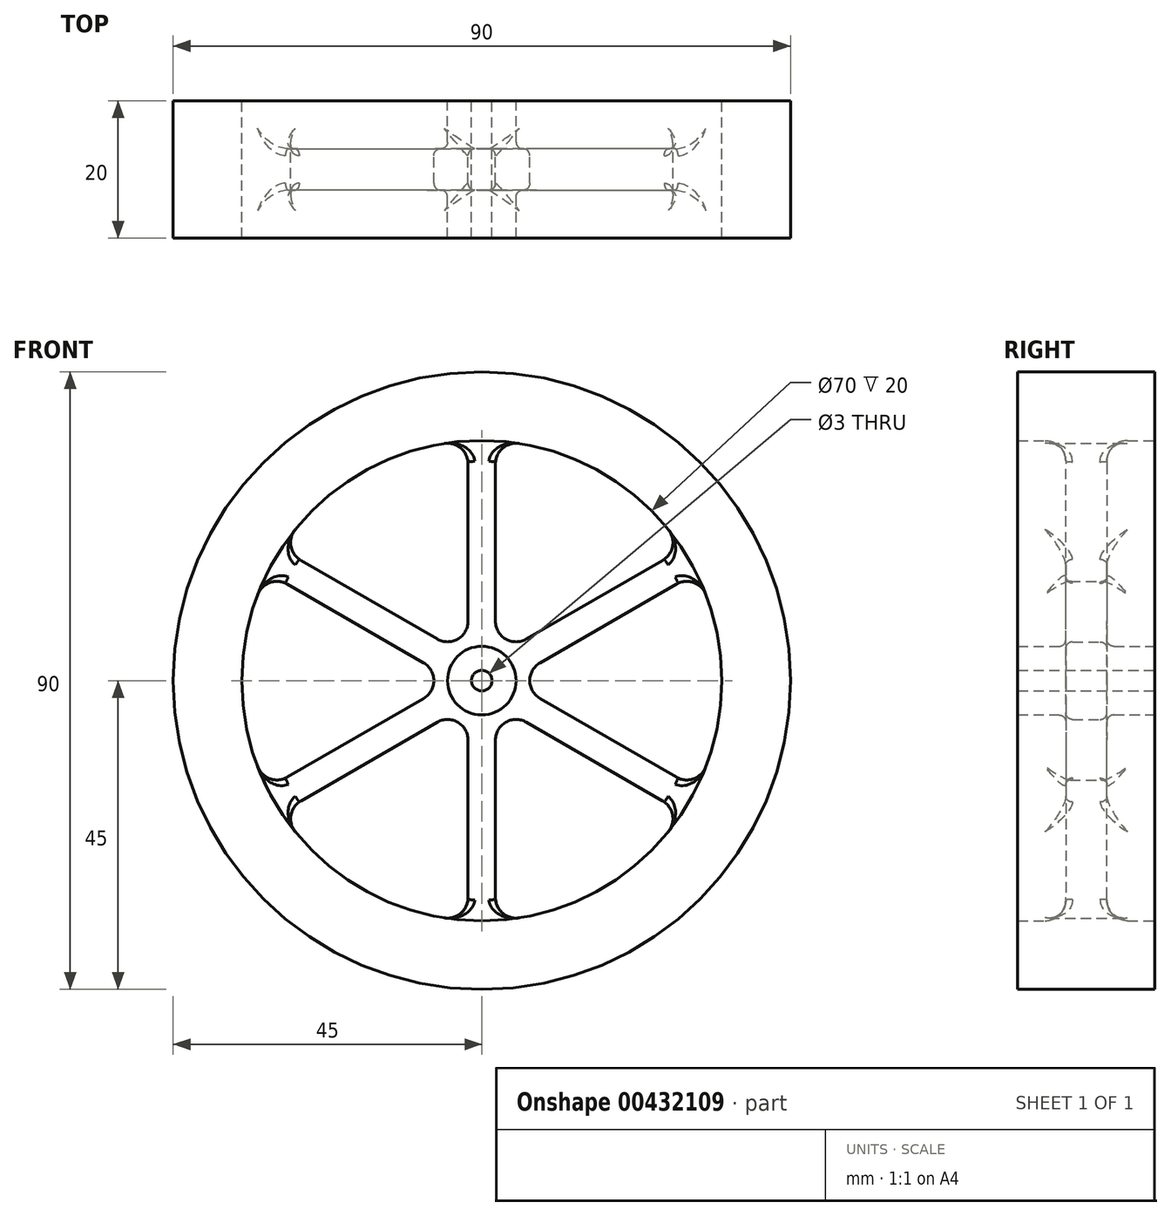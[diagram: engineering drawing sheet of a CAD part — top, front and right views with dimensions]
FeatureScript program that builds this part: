
annotation { "Feature Type Name" : "Feature", "Feature Type Description" : "" }
export const myFeature = defineFeature(function(context is Context, id is Id, definition is map)
    precondition{}
    {
        {
            var Q0;
            Q0=qCreatedBy(makeId("Front.planeOp"),FACE);
            var sketch = newSketch(context, id + "F0", { "sketchPlane" : qUnion([Q0])});
            skCircle(sketch, "E0", {"center": v(0, 0) * mm, "radius": 45 * mm});
            skArc(sketch, "E1", {"start": v(-32.67, 12.55) * mm, "mid": v(-35, 0) * mm, "end": v(-32.67, -12.55) * mm});
            skLineSegment(sketch, "E2.0", {"start": v(2, 8.66) * mm, "end": v(2, 31.6) * mm});
            skLineSegment(sketch, "E3.0", {"start": v(-2, 8.66) * mm, "end": v(-2, 31.6) * mm});
            skLineSegment(sketch, "E4.1.0", {"start": v(-8.5, 2.6) * mm, "end": v(-28.37, 14.07) * mm});
            skLineSegment(sketch, "E4.1.1", {"start": v(-6.5, 6.06) * mm, "end": v(-26.37, 17.54) * mm});
            skLineSegment(sketch, "E4.2.0", {"start": v(-6.5, -6.06) * mm, "end": v(-26.37, -17.54) * mm});
            skLineSegment(sketch, "E4.2.1", {"start": v(-8.5, -2.6) * mm, "end": v(-28.37, -14.07) * mm});
            skLineSegment(sketch, "E4.3.0", {"start": v(2, -8.66) * mm, "end": v(2, -31.6) * mm});
            skLineSegment(sketch, "E4.3.1", {"start": v(-2, -8.66) * mm, "end": v(-2, -31.6) * mm});
            skLineSegment(sketch, "E4.4.0", {"start": v(8.5, -2.6) * mm, "end": v(28.37, -14.07) * mm});
            skLineSegment(sketch, "E4.4.1", {"start": v(6.5, -6.06) * mm, "end": v(26.37, -17.54) * mm});
            skLineSegment(sketch, "E4.5.0", {"start": v(6.5, 6.06) * mm, "end": v(26.37, 17.54) * mm});
            skLineSegment(sketch, "E4.5.1", {"start": v(8.5, 2.6) * mm, "end": v(28.37, 14.07) * mm});
            skArc(sketch, "E5.filletArc", {"start": v(2, 8.66) * mm, "mid": v(3.5, 6.06) * mm, "end": v(6.5, 6.06) * mm});
            skArc(sketch, "E6.filletArc", {"start": v(-6.5, 6.06) * mm, "mid": v(-3.5, 6.06) * mm, "end": v(-2, 8.66) * mm});
            skArc(sketch, "E7.filletArc", {"start": v(-8.5, -2.6) * mm, "mid": v(-7, 0) * mm, "end": v(-8.5, 2.6) * mm});
            skArc(sketch, "E8.filletArc", {"start": v(-2, -8.66) * mm, "mid": v(-3.5, -6.06) * mm, "end": v(-6.5, -6.06) * mm});
            skArc(sketch, "E9.filletArc", {"start": v(6.5, -6.06) * mm, "mid": v(3.5, -6.06) * mm, "end": v(2, -8.66) * mm});
            skArc(sketch, "E10.filletArc", {"start": v(8.5, 2.6) * mm, "mid": v(7, 0) * mm, "end": v(8.5, -2.6) * mm});
            skArc(sketch, "E11.trimOffspring", {"start": v(-5.47, 34.57) * mm, "mid": v(-17.5, 30.31) * mm, "end": v(-27.2, 22.02) * mm});
            skArc(sketch, "E12.trimOffspring", {"start": v(27.2, 22.02) * mm, "mid": v(17.5, 30.31) * mm, "end": v(5.47, 34.57) * mm});
            skArc(sketch, "E13.trimOffspring", {"start": v(32.67, -12.55) * mm, "mid": v(35, 0) * mm, "end": v(32.67, 12.55) * mm});
            skArc(sketch, "E14.trimOffspring", {"start": v(5.47, -34.57) * mm, "mid": v(17.5, -30.31) * mm, "end": v(27.2, -22.02) * mm});
            skArc(sketch, "E15.trimOffspring", {"start": v(-27.2, -22.02) * mm, "mid": v(-17.5, -30.31) * mm, "end": v(-5.47, -34.57) * mm});
            skArc(sketch, "E16.filletArc", {"start": v(-27.2, 22.02) * mm, "mid": v(-27.82, 19.59) * mm, "end": v(-26.37, 17.54) * mm});
            skArc(sketch, "E17.filletArc", {"start": v(-2, 31.6) * mm, "mid": v(-3.05, 33.89) * mm, "end": v(-5.47, 34.57) * mm});
            skArc(sketch, "E18.filletArc", {"start": v(5.47, 34.57) * mm, "mid": v(3.05, 33.89) * mm, "end": v(2, 31.6) * mm});
            skArc(sketch, "E19.filletArc", {"start": v(26.37, 17.54) * mm, "mid": v(27.82, 19.59) * mm, "end": v(27.2, 22.02) * mm});
            skArc(sketch, "E20.filletArc", {"start": v(32.67, 12.55) * mm, "mid": v(30.87, 14.3) * mm, "end": v(28.37, 14.07) * mm});
            skArc(sketch, "E21.filletArc", {"start": v(28.37, -14.07) * mm, "mid": v(30.87, -14.3) * mm, "end": v(32.67, -12.55) * mm});
            skArc(sketch, "E22.filletArc", {"start": v(27.2, -22.02) * mm, "mid": v(27.82, -19.59) * mm, "end": v(26.37, -17.54) * mm});
            skArc(sketch, "E23.filletArc", {"start": v(2, -31.6) * mm, "mid": v(3.05, -33.89) * mm, "end": v(5.47, -34.57) * mm});
            skArc(sketch, "E24.filletArc", {"start": v(-5.47, -34.57) * mm, "mid": v(-3.05, -33.89) * mm, "end": v(-2, -31.6) * mm});
            skArc(sketch, "E25.filletArc", {"start": v(-26.37, -17.54) * mm, "mid": v(-27.82, -19.59) * mm, "end": v(-27.2, -22.02) * mm});
            skArc(sketch, "E26.filletArc", {"start": v(-32.67, -12.55) * mm, "mid": v(-30.87, -14.3) * mm, "end": v(-28.37, -14.07) * mm});
            skArc(sketch, "E27.filletArc", {"start": v(-28.37, 14.07) * mm, "mid": v(-30.87, 14.3) * mm, "end": v(-32.67, 12.55) * mm});
            skSolve(sketch);
        }
        {
            var Q0;
            Q0 = qSketchRegion(id + "F0", true);
            extrude(context, id + "F1", {"entities" : qUnion([Q0]), "depth" : 20 * mm});
        }
        {
            var Q0;
            Q0=makeQuery(id+"F1.opExtrude","CAP_FACE",FACE,{"disambiguationData":[OSD([sQuery(id+"F0.wireOp",EDGE,"E0"),sQuery(id+"F0.wireOp",EDGE,"E1"),sQuery(id+"F0.wireOp",EDGE,"E2.0"),sQuery(id+"F0.wireOp",EDGE,"E3.0"),sQuery(id+"F0.wireOp",EDGE,"E4.1.0"),sQuery(id+"F0.wireOp",EDGE,"E4.1.1"),sQuery(id+"F0.wireOp",EDGE,"E4.2.0"),sQuery(id+"F0.wireOp",EDGE,"E4.2.1"),sQuery(id+"F0.wireOp",EDGE,"E4.3.0"),sQuery(id+"F0.wireOp",EDGE,"E4.3.1"),sQuery(id+"F0.wireOp",EDGE,"E4.4.0"),sQuery(id+"F0.wireOp",EDGE,"E4.4.1"),sQuery(id+"F0.wireOp",EDGE,"E4.5.0"),sQuery(id+"F0.wireOp",EDGE,"E4.5.1"),sQuery(id+"F0.wireOp",EDGE,"E5.filletArc"),sQuery(id+"F0.wireOp",EDGE,"E6.filletArc"),sQuery(id+"F0.wireOp",EDGE,"E7.filletArc"),sQuery(id+"F0.wireOp",EDGE,"E8.filletArc"),sQuery(id+"F0.wireOp",EDGE,"E9.filletArc"),sQuery(id+"F0.wireOp",EDGE,"E10.filletArc"),sQuery(id+"F0.wireOp",EDGE,"E11.trimOffspring"),sQuery(id+"F0.wireOp",EDGE,"E12.trimOffspring"),sQuery(id+"F0.wireOp",EDGE,"E13.trimOffspring"),sQuery(id+"F0.wireOp",EDGE,"E14.trimOffspring"),sQuery(id+"F0.wireOp",EDGE,"E15.trimOffspring"),sQuery(id+"F0.wireOp",EDGE,"E16.filletArc"),sQuery(id+"F0.wireOp",EDGE,"E17.filletArc"),sQuery(id+"F0.wireOp",EDGE,"E18.filletArc"),sQuery(id+"F0.wireOp",EDGE,"E19.filletArc"),sQuery(id+"F0.wireOp",EDGE,"E20.filletArc"),sQuery(id+"F0.wireOp",EDGE,"E21.filletArc"),sQuery(id+"F0.wireOp",EDGE,"E22.filletArc"),sQuery(id+"F0.wireOp",EDGE,"E23.filletArc"),sQuery(id+"F0.wireOp",EDGE,"E24.filletArc"),sQuery(id+"F0.wireOp",EDGE,"E25.filletArc"),sQuery(id+"F0.wireOp",EDGE,"E26.filletArc"),sQuery(id+"F0.wireOp",EDGE,"E27.filletArc")])],"isStart":false});
            var sketch = newSketch(context, id + "F2", { "sketchPlane" : qUnion([Q0])});
            skCircle(sketch, "E28", {"center": v(0, 0) * mm, "radius": 35 * mm});
            skSolve(sketch);
        }
        {
            var Q0;
            Q0 = qSketchRegion(id + "F2", true);
            extrude(context, id + "F3", {"entities" : qUnion([Q0]), "operationType" : NewBodyOperationType.REMOVE, "oppositeDirection" : true, "depth" : 7 * mm});
        }
        {
            var Q0;
            Q0=makeQuery(id+"F1.opExtrude","CAP_FACE",FACE,{"disambiguationData":[OSD([sQuery(id+"F0.wireOp",EDGE,"E0"),sQuery(id+"F0.wireOp",EDGE,"E1"),sQuery(id+"F0.wireOp",EDGE,"E2.0"),sQuery(id+"F0.wireOp",EDGE,"E3.0"),sQuery(id+"F0.wireOp",EDGE,"E4.1.0"),sQuery(id+"F0.wireOp",EDGE,"E4.1.1"),sQuery(id+"F0.wireOp",EDGE,"E4.2.0"),sQuery(id+"F0.wireOp",EDGE,"E4.2.1"),sQuery(id+"F0.wireOp",EDGE,"E4.3.0"),sQuery(id+"F0.wireOp",EDGE,"E4.3.1"),sQuery(id+"F0.wireOp",EDGE,"E4.4.0"),sQuery(id+"F0.wireOp",EDGE,"E4.4.1"),sQuery(id+"F0.wireOp",EDGE,"E4.5.0"),sQuery(id+"F0.wireOp",EDGE,"E4.5.1"),sQuery(id+"F0.wireOp",EDGE,"E5.filletArc"),sQuery(id+"F0.wireOp",EDGE,"E6.filletArc"),sQuery(id+"F0.wireOp",EDGE,"E7.filletArc"),sQuery(id+"F0.wireOp",EDGE,"E8.filletArc"),sQuery(id+"F0.wireOp",EDGE,"E9.filletArc"),sQuery(id+"F0.wireOp",EDGE,"E10.filletArc"),sQuery(id+"F0.wireOp",EDGE,"E11.trimOffspring"),sQuery(id+"F0.wireOp",EDGE,"E12.trimOffspring"),sQuery(id+"F0.wireOp",EDGE,"E13.trimOffspring"),sQuery(id+"F0.wireOp",EDGE,"E14.trimOffspring"),sQuery(id+"F0.wireOp",EDGE,"E15.trimOffspring"),sQuery(id+"F0.wireOp",EDGE,"E16.filletArc"),sQuery(id+"F0.wireOp",EDGE,"E17.filletArc"),sQuery(id+"F0.wireOp",EDGE,"E18.filletArc"),sQuery(id+"F0.wireOp",EDGE,"E19.filletArc"),sQuery(id+"F0.wireOp",EDGE,"E20.filletArc"),sQuery(id+"F0.wireOp",EDGE,"E21.filletArc"),sQuery(id+"F0.wireOp",EDGE,"E22.filletArc"),sQuery(id+"F0.wireOp",EDGE,"E23.filletArc"),sQuery(id+"F0.wireOp",EDGE,"E24.filletArc"),sQuery(id+"F0.wireOp",EDGE,"E25.filletArc"),sQuery(id+"F0.wireOp",EDGE,"E26.filletArc"),sQuery(id+"F0.wireOp",EDGE,"E27.filletArc")])],"isStart":true});
            var sketch = newSketch(context, id + "F4", { "sketchPlane" : qUnion([Q0])});
            skCircle(sketch, "E29", {"center": v(0, 0) * mm, "radius": 35 * mm});
            skSolve(sketch);
        }
        {
            var Q0;
            Q0 = qSketchRegion(id + "F4", true);
            extrude(context, id + "F5", {"entities" : qUnion([Q0]), "operationType" : NewBodyOperationType.REMOVE, "oppositeDirection" : true, "depth" : 7 * mm});
        }
        {
            var Q0;
            {var subQ0=sQuery(id+"F4.wireOp",EDGE,"E29");Q0=makeQuery(id+"F5.boolean.opBoolean","COPY",EDGE,{"disambiguationData":[TD([makeQuery(id+"F1.opExtrude","SWEPT_FACE",FACE,{"disambiguationData":[OSD([sQuery(id+"F0.wireOp",EDGE,"E23.filletArc")])]})])],"derivedFrom":makeQuery(id+"F5.opExtrude","CAP_EDGE",EDGE,{"disambiguationData":[OSD([subQ0])],"isStart":false})});}
            var Q1;
            {var subQ0=sQuery(id+"F4.wireOp",EDGE,"E29");Q1=makeQuery(id+"F5.boolean.opBoolean","COPY",EDGE,{"disambiguationData":[TD([makeQuery(id+"F1.opExtrude","SWEPT_FACE",FACE,{"disambiguationData":[OSD([sQuery(id+"F0.wireOp",EDGE,"E21.filletArc")])]})])],"derivedFrom":makeQuery(id+"F5.opExtrude","CAP_EDGE",EDGE,{"disambiguationData":[OSD([subQ0])],"isStart":false})});}
            var Q2;
            {var subQ0=sQuery(id+"F4.wireOp",EDGE,"E29");Q2=makeQuery(id+"F5.boolean.opBoolean","COPY",EDGE,{"disambiguationData":[TD([makeQuery(id+"F1.opExtrude","SWEPT_FACE",FACE,{"disambiguationData":[OSD([sQuery(id+"F0.wireOp",EDGE,"E19.filletArc")])]})])],"derivedFrom":makeQuery(id+"F5.opExtrude","CAP_EDGE",EDGE,{"disambiguationData":[OSD([subQ0])],"isStart":false})});}
            var Q3;
            {var subQ0=sQuery(id+"F4.wireOp",EDGE,"E29");Q3=makeQuery(id+"F5.boolean.opBoolean","COPY",EDGE,{"disambiguationData":[TD([makeQuery(id+"F1.opExtrude","SWEPT_FACE",FACE,{"disambiguationData":[OSD([sQuery(id+"F0.wireOp",EDGE,"E17.filletArc")])]})])],"derivedFrom":makeQuery(id+"F5.opExtrude","CAP_EDGE",EDGE,{"disambiguationData":[OSD([subQ0])],"isStart":false})});}
            var Q4;
            {var subQ0=sQuery(id+"F4.wireOp",EDGE,"E29");Q4=makeQuery(id+"F5.boolean.opBoolean","COPY",EDGE,{"disambiguationData":[TD([makeQuery(id+"F1.opExtrude","SWEPT_FACE",FACE,{"disambiguationData":[OSD([sQuery(id+"F0.wireOp",EDGE,"E16.filletArc")])]})])],"derivedFrom":makeQuery(id+"F5.opExtrude","CAP_EDGE",EDGE,{"disambiguationData":[OSD([subQ0])],"isStart":false})});}
            var Q5;
            {var subQ0=sQuery(id+"F4.wireOp",EDGE,"E29");Q5=makeQuery(id+"F5.boolean.opBoolean","COPY",EDGE,{"disambiguationData":[TD([makeQuery(id+"F1.opExtrude","SWEPT_FACE",FACE,{"disambiguationData":[OSD([sQuery(id+"F0.wireOp",EDGE,"E25.filletArc")])]})])],"derivedFrom":makeQuery(id+"F5.opExtrude","CAP_EDGE",EDGE,{"disambiguationData":[OSD([subQ0])],"isStart":false})});}
            var Q6;
            {var subQ0=sQuery(id+"F2.wireOp",EDGE,"E28");Q6=makeQuery(id+"F3.boolean.opBoolean","COPY",EDGE,{"disambiguationData":[TD([makeQuery(id+"F1.opExtrude","SWEPT_FACE",FACE,{"disambiguationData":[OSD([sQuery(id+"F0.wireOp",EDGE,"E21.filletArc")])]})])],"derivedFrom":makeQuery(id+"F3.opExtrude","CAP_EDGE",EDGE,{"disambiguationData":[OSD([subQ0])],"isStart":false})});}
            var Q7;
            {var subQ0=sQuery(id+"F2.wireOp",EDGE,"E28");Q7=makeQuery(id+"F3.boolean.opBoolean","COPY",EDGE,{"disambiguationData":[TD([makeQuery(id+"F1.opExtrude","SWEPT_FACE",FACE,{"disambiguationData":[OSD([sQuery(id+"F0.wireOp",EDGE,"E23.filletArc")])]})])],"derivedFrom":makeQuery(id+"F3.opExtrude","CAP_EDGE",EDGE,{"disambiguationData":[OSD([subQ0])],"isStart":false})});}
            var Q8;
            {var subQ0=sQuery(id+"F2.wireOp",EDGE,"E28");Q8=makeQuery(id+"F3.boolean.opBoolean","COPY",EDGE,{"disambiguationData":[TD([makeQuery(id+"F1.opExtrude","SWEPT_FACE",FACE,{"disambiguationData":[OSD([sQuery(id+"F0.wireOp",EDGE,"E25.filletArc")])]})])],"derivedFrom":makeQuery(id+"F3.opExtrude","CAP_EDGE",EDGE,{"disambiguationData":[OSD([subQ0])],"isStart":false})});}
            var Q9;
            {var subQ0=sQuery(id+"F2.wireOp",EDGE,"E28");Q9=makeQuery(id+"F3.boolean.opBoolean","COPY",EDGE,{"disambiguationData":[TD([makeQuery(id+"F1.opExtrude","SWEPT_FACE",FACE,{"disambiguationData":[OSD([sQuery(id+"F0.wireOp",EDGE,"E16.filletArc")])]})])],"derivedFrom":makeQuery(id+"F3.opExtrude","CAP_EDGE",EDGE,{"disambiguationData":[OSD([subQ0])],"isStart":false})});}
            var Q10;
            {var subQ0=sQuery(id+"F2.wireOp",EDGE,"E28");Q10=makeQuery(id+"F3.boolean.opBoolean","COPY",EDGE,{"disambiguationData":[TD([makeQuery(id+"F1.opExtrude","SWEPT_FACE",FACE,{"disambiguationData":[OSD([sQuery(id+"F0.wireOp",EDGE,"E17.filletArc")])]})])],"derivedFrom":makeQuery(id+"F3.opExtrude","CAP_EDGE",EDGE,{"disambiguationData":[OSD([subQ0])],"isStart":false})});}
            var Q11;
            {var subQ0=sQuery(id+"F2.wireOp",EDGE,"E28");Q11=makeQuery(id+"F3.boolean.opBoolean","COPY",EDGE,{"disambiguationData":[TD([makeQuery(id+"F1.opExtrude","SWEPT_FACE",FACE,{"disambiguationData":[OSD([sQuery(id+"F0.wireOp",EDGE,"E19.filletArc")])]})])],"derivedFrom":makeQuery(id+"F3.opExtrude","CAP_EDGE",EDGE,{"disambiguationData":[OSD([subQ0])],"isStart":false})});}
            fillet(context, id + "F6", {"entities" : qUnion([Q0, Q1, Q2, Q3, Q4, Q5, Q6, Q7, Q8, Q9, Q10, Q11]), "radius" : 3 * mm, "tangentPropagation" : true, "allowEdgeOverflow" : false});
        }
        {
            var Q0;
            Q0=makeQuery(id+"F5.boolean.opBoolean","INTERSECT",EDGE,{"derivedFrom":[makeQuery(id+"F1.opExtrude","SWEPT_FACE",FACE,{"disambiguationData":[OSD([sQuery(id+"F0.wireOp",EDGE,"E3.0")])]}),makeQuery(id+"F5.opExtrude","CAP_FACE",FACE,{"disambiguationData":[OSD([sQuery(id+"F4.wireOp",EDGE,"E29")])],"isStart":false})]});
            var Q1;
            Q1=makeQuery(id+"F5.boolean.opBoolean","INTERSECT",EDGE,{"derivedFrom":[makeQuery(id+"F1.opExtrude","SWEPT_FACE",FACE,{"disambiguationData":[OSD([sQuery(id+"F0.wireOp",EDGE,"E4.1.0")])]}),makeQuery(id+"F5.opExtrude","CAP_FACE",FACE,{"disambiguationData":[OSD([sQuery(id+"F4.wireOp",EDGE,"E29")])],"isStart":false})]});
            var Q2;
            Q2=makeQuery(id+"F5.boolean.opBoolean","INTERSECT",EDGE,{"derivedFrom":[makeQuery(id+"F1.opExtrude","SWEPT_FACE",FACE,{"disambiguationData":[OSD([sQuery(id+"F0.wireOp",EDGE,"E4.2.0")])]}),makeQuery(id+"F5.opExtrude","CAP_FACE",FACE,{"disambiguationData":[OSD([sQuery(id+"F4.wireOp",EDGE,"E29")])],"isStart":false})]});
            var Q3;
            Q3=makeQuery(id+"F5.boolean.opBoolean","INTERSECT",EDGE,{"derivedFrom":[makeQuery(id+"F1.opExtrude","SWEPT_FACE",FACE,{"disambiguationData":[OSD([sQuery(id+"F0.wireOp",EDGE,"E4.3.0")])]}),makeQuery(id+"F5.opExtrude","CAP_FACE",FACE,{"disambiguationData":[OSD([sQuery(id+"F4.wireOp",EDGE,"E29")])],"isStart":false})]});
            var Q4;
            Q4=makeQuery(id+"F5.boolean.opBoolean","INTERSECT",EDGE,{"derivedFrom":[makeQuery(id+"F1.opExtrude","SWEPT_FACE",FACE,{"disambiguationData":[OSD([sQuery(id+"F0.wireOp",EDGE,"E4.5.1")])]}),makeQuery(id+"F5.opExtrude","CAP_FACE",FACE,{"disambiguationData":[OSD([sQuery(id+"F4.wireOp",EDGE,"E29")])],"isStart":false})]});
            var Q5;
            Q5=makeQuery(id+"F5.boolean.opBoolean","INTERSECT",EDGE,{"derivedFrom":[makeQuery(id+"F1.opExtrude","SWEPT_FACE",FACE,{"disambiguationData":[OSD([sQuery(id+"F0.wireOp",EDGE,"E2.0")])]}),makeQuery(id+"F5.opExtrude","CAP_FACE",FACE,{"disambiguationData":[OSD([sQuery(id+"F4.wireOp",EDGE,"E29")])],"isStart":false})]});
            var Q6;
            Q6=makeQuery(id+"F3.boolean.opBoolean","INTERSECT",EDGE,{"derivedFrom":[makeQuery(id+"F1.opExtrude","SWEPT_FACE",FACE,{"disambiguationData":[OSD([sQuery(id+"F0.wireOp",EDGE,"E3.0")])]}),makeQuery(id+"F3.opExtrude","CAP_FACE",FACE,{"disambiguationData":[OSD([sQuery(id+"F2.wireOp",EDGE,"E28")])],"isStart":false})]});
            var Q7;
            Q7=makeQuery(id+"F3.boolean.opBoolean","INTERSECT",EDGE,{"derivedFrom":[makeQuery(id+"F1.opExtrude","SWEPT_FACE",FACE,{"disambiguationData":[OSD([sQuery(id+"F0.wireOp",EDGE,"E4.5.0")])]}),makeQuery(id+"F3.opExtrude","CAP_FACE",FACE,{"disambiguationData":[OSD([sQuery(id+"F2.wireOp",EDGE,"E28")])],"isStart":false})]});
            var Q8;
            Q8=makeQuery(id+"F3.boolean.opBoolean","INTERSECT",EDGE,{"derivedFrom":[makeQuery(id+"F1.opExtrude","SWEPT_FACE",FACE,{"disambiguationData":[OSD([sQuery(id+"F0.wireOp",EDGE,"E4.4.0")])]}),makeQuery(id+"F3.opExtrude","CAP_FACE",FACE,{"disambiguationData":[OSD([sQuery(id+"F2.wireOp",EDGE,"E28")])],"isStart":false})]});
            var Q9;
            Q9=makeQuery(id+"F3.boolean.opBoolean","INTERSECT",EDGE,{"derivedFrom":[makeQuery(id+"F1.opExtrude","SWEPT_FACE",FACE,{"disambiguationData":[OSD([sQuery(id+"F0.wireOp",EDGE,"E4.4.1")])]}),makeQuery(id+"F3.opExtrude","CAP_FACE",FACE,{"disambiguationData":[OSD([sQuery(id+"F2.wireOp",EDGE,"E28")])],"isStart":false})]});
            var Q10;
            Q10=makeQuery(id+"F3.boolean.opBoolean","INTERSECT",EDGE,{"derivedFrom":[makeQuery(id+"F1.opExtrude","SWEPT_FACE",FACE,{"disambiguationData":[OSD([sQuery(id+"F0.wireOp",EDGE,"E4.3.1")])]}),makeQuery(id+"F3.opExtrude","CAP_FACE",FACE,{"disambiguationData":[OSD([sQuery(id+"F2.wireOp",EDGE,"E28")])],"isStart":false})]});
            var Q11;
            Q11=makeQuery(id+"F3.boolean.opBoolean","INTERSECT",EDGE,{"derivedFrom":[makeQuery(id+"F1.opExtrude","SWEPT_FACE",FACE,{"disambiguationData":[OSD([sQuery(id+"F0.wireOp",EDGE,"E4.2.1")])]}),makeQuery(id+"F3.opExtrude","CAP_FACE",FACE,{"disambiguationData":[OSD([sQuery(id+"F2.wireOp",EDGE,"E28")])],"isStart":false})]});
            fillet(context, id + "F7", {"entities" : qUnion([Q0, Q1, Q2, Q3, Q4, Q5, Q6, Q7, Q8, Q9, Q10, Q11]), "radius" : 1 * mm, "tangentPropagation" : true, "allowEdgeOverflow" : false});
        }
        {
            var Q0;
            Q0=qCreatedBy(makeId("Front.planeOp"),FACE);
            var sketch = newSketch(context, id + "F8", { "sketchPlane" : qUnion([Q0])});
            skCircle(sketch, "E30", {"center": v(0, 0) * mm, "radius": 5 * mm});
            skSolve(sketch);
        }
        {
            var Q0;
            Q0 = qSketchRegion(id + "F8", true);
            extrude(context, id + "F9", {"entities" : qUnion([Q0]), "operationType" : NewBodyOperationType.ADD, "depth" : 20 * mm});
        }
        {
            var Q0;
            Q0=makeQuery(id+"F9.opExtrude","CAP_FACE",FACE,{"disambiguationData":[OSD([sQuery(id+"F8.wireOp",EDGE,"E30")])],"isStart":true});
            var sketch = newSketch(context, id + "F10", { "sketchPlane" : qUnion([Q0])});
            skCircle(sketch, "E31", {"center": v(0, 0) * mm, "radius": 1.5 * mm});
            skSolve(sketch);
        }
        {
            var Q0;
            Q0 = qSketchRegion(id + "F10", true);
            extrude(context, id + "F11", {"entities" : qUnion([Q0]), "operationType" : NewBodyOperationType.REMOVE, "endBound" : BoundingType.THROUGH_ALL, "oppositeDirection" : true, "depth" : 25 * mm});
        }
        {
            var Q0;
            Q0=makeQuery(id+"F9.boolean.opBoolean","INTERSECT",EDGE,{"derivedFrom":[makeQuery(id+"F5.boolean.opBoolean","COPY",FACE,{"derivedFrom":makeQuery(id+"F5.opExtrude","CAP_FACE",FACE,{"disambiguationData":[OSD([sQuery(id+"F4.wireOp",EDGE,"E29")])],"isStart":false})}),makeQuery(id+"F9.opExtrude","SWEPT_FACE",FACE,{"disambiguationData":[OSD([sQuery(id+"F8.wireOp",EDGE,"E30")])]})]});
            var Q1;
            Q1=makeQuery(id+"F9.boolean.opBoolean","INTERSECT",EDGE,{"derivedFrom":[makeQuery(id+"F3.boolean.opBoolean","COPY",FACE,{"derivedFrom":makeQuery(id+"F3.opExtrude","CAP_FACE",FACE,{"disambiguationData":[OSD([sQuery(id+"F2.wireOp",EDGE,"E28")])],"isStart":false})}),makeQuery(id+"F9.opExtrude","SWEPT_FACE",FACE,{"disambiguationData":[OSD([sQuery(id+"F8.wireOp",EDGE,"E30")])]})]});
            fillet(context, id + "F12", {"entities" : qUnion([Q0, Q1]), "radius" : 1 * mm, "tangentPropagation" : true, "allowEdgeOverflow" : false});
        }
    });
